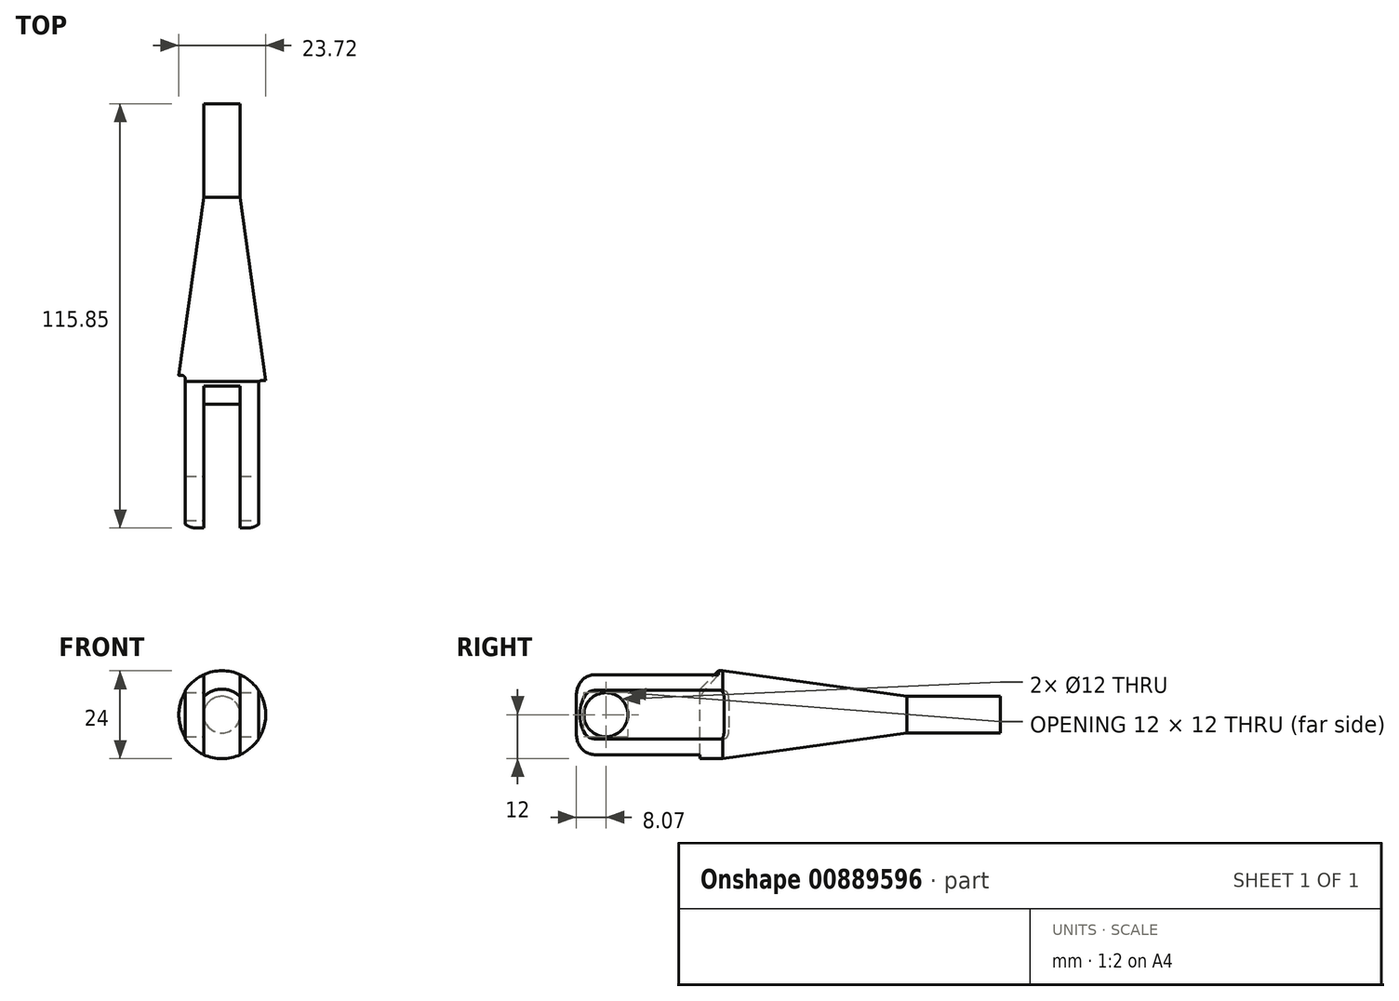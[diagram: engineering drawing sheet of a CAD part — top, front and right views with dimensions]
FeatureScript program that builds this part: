
annotation { "Feature Type Name" : "Feature", "Feature Type Description" : "" }
export const myFeature = defineFeature(function(context is Context, id is Id, definition is map)
    precondition{}
    {
        {
            var Q0;
            Q0=qCreatedBy(makeId("Right.planeOp"),FACE);
            var sketch = newSketch(context, id + "F0", { "sketchPlane" : qUnion([Q0])});
            skLineSegment(sketch, "E0", {"start": v(-22.63, 0) * mm, "end": v(-22.63, 12) * mm});
            skLineSegment(sketch, "E1", {"start": v(-22.63, 12) * mm, "end": v(17.37, 12) * mm});
            skLineSegment(sketch, "E2", {"start": v(93.22, 5) * mm, "end": v(93.22, 0) * mm});
            skLineSegment(sketch, "E3", {"start": v(93.22, 0) * mm, "end": v(-22.63, 0) * mm});
            skLineSegment(sketch, "E4", {"start": v(93.22, 5) * mm, "end": v(67.7, 5) * mm});
            skLineSegment(sketch, "E5", {"start": v(67.7, 5) * mm, "end": v(17.37, 12) * mm});
            skSolve(sketch);
        }
        {
            var Q0;
            Q0=makeQuery(id+"F0.imprint","IMPRINT",FACE,{"disambiguationData":[TD([[makeQuery(id+"F0.imprint","IMPRINT",EDGE,{"derivedFrom":sQuery(id+"F0.wireOp",EDGE,"E0")}),-1.0]])]});
            var Q1;
            Q1=sQuery(id+"F0.wireOp",EDGE,"E3");
            revolve(context, id + "F1", {"surfaceOperationType" : NewSurfaceOperationType.NEW, "entities" : qUnion([Q0]), "axis" : qUnion([Q1]), "revolveType" : RevolveType.FULL});
        }
        {
            var Q0;
            Q0=qCreatedBy(makeId("Top.planeOp"),FACE);
            cPlane(context, id + "F2", {"entities" : qUnion([Q0]), "cplaneType" : CPlaneType.OFFSET, "offset" : 25 * mm, "width" : 150 * mm, "height" : 150 * mm});
        }
        {
            var Q0;
            Q0=qCreatedBy(id+"F2.planeOp",FACE);
            var sketch = newSketch(context, id + "F3", { "sketchPlane" : qUnion([Q0])});
            skLineSegment(sketch, "E6", {"start": v(-10, 19.06) * mm, "end": v(-10, -31.43) * mm});
            skLineSegment(sketch, "E7", {"start": v(10, -31.43) * mm, "end": v(10, 17.7) * mm});
            skLineSegment(sketch, "E8", {"start": v(10, 17.7) * mm, "end": v(28.05, 17.7) * mm});
            skLineSegment(sketch, "E9", {"start": v(28.05, 17.7) * mm, "end": v(28.05, -44.11) * mm});
            skLineSegment(sketch, "E10", {"start": v(28.05, -44.11) * mm, "end": v(-18.09, -44.11) * mm});
            skLineSegment(sketch, "E11", {"start": v(-18.09, -44.11) * mm, "end": v(-18.09, 18.88) * mm});
            skLineSegment(sketch, "E12", {"start": v(-18.09, 18.88) * mm, "end": v(-10, 19.06) * mm});
            skLineSegment(sketch, "E13", {"start": v(-10, -31.43) * mm, "end": v(-5, -31.43) * mm});
            skLineSegment(sketch, "E14", {"start": v(-5, -31.43) * mm, "end": v(-5, 11.16) * mm});
            skLineSegment(sketch, "E15", {"start": v(-5, 11.16) * mm, "end": v(5, 11.16) * mm});
            skLineSegment(sketch, "E16", {"start": v(5, 11.16) * mm, "end": v(5, -31.43) * mm});
            skLineSegment(sketch, "E17", {"start": v(5, -31.43) * mm, "end": v(10, -31.43) * mm});
            skSolve(sketch);
        }
        {
            var Q0;
            Q0=makeQuery(id+"F3.imprint","IMPRINT",FACE,{"disambiguationData":[TD([[makeQuery(id+"F3.imprint","IMPRINT",EDGE,{"derivedFrom":sQuery(id+"F3.wireOp",EDGE,"E6")}),-1.0]])]});
            extrude(context, id + "F4", {"entities" : qUnion([Q0]), "operationType" : NewBodyOperationType.REMOVE, "endBound" : BoundingType.THROUGH_ALL, "oppositeDirection" : true, "depth" : 25 * mm, "offsetDistance" : 25 * mm});
        }
        {
            var Q0;
            Q0=makeQuery(id+"F4.boolean.opBoolean","COPY",FACE,{"derivedFrom":makeQuery(id+"F4.opExtrude","SWEPT_FACE",FACE,{"disambiguationData":[OSD([sQuery(id+"F3.wireOp",EDGE,"E7")])]})});
            var sketch = newSketch(context, id + "F5", { "sketchPlane" : qUnion([Q0])});
            skCircle(sketch, "E18", {"center": v(-14.56, 0) * mm, "radius": 6 * mm});
            skSolve(sketch);
        }
        {
            var Q0;
            Q0=makeQuery(id+"F5.imprint","IMPRINT",FACE,{"disambiguationData":[TD([[makeQuery(id+"F5.imprint","IMPRINT",EDGE,{"derivedFrom":sQuery(id+"F5.wireOp",EDGE,"E18")}),1.0]])]});
            extrude(context, id + "F6", {"entities" : qUnion([Q0]), "operationType" : NewBodyOperationType.REMOVE, "endBound" : BoundingType.THROUGH_ALL, "oppositeDirection" : true, "depth" : 25 * mm, "offsetDistance" : 25 * mm});
        }
        {
            var Q0;
            Q0=makeQuery(id+"F4.boolean.opBoolean","INTERSECT",EDGE,{"disambiguationData":[OD(1.0)],"derivedFrom":[makeQuery(id+"F1.opRevolve","SWEPT_FACE",FACE,{"disambiguationData":[OSD([sQuery(id+"F0.wireOp",EDGE,"E1")])]}),makeQuery(id+"F4.opExtrude","SWEPT_FACE",FACE,{"disambiguationData":[OSD([sQuery(id+"F3.wireOp",EDGE,"E15")])]})]});
            chamfer(context, id + "F7", {"entities" : qUnion([Q0]), "width" : 5 * mm, "tangentPropagation" : true});
        }
        {
            var Q0;
            {var subQ0=sQuery(id+"F0.wireOp",EDGE,"E0");var subQ1=sQuery(id+"F0.wireOp",EDGE,"E1");Q0=makeQuery(id+"F4.boolean.opBoolean","SPLIT",EDGE,{"disambiguationData":[TD([makeQuery(id+"F1.opRevolve","SWEPT_FACE",FACE,{"disambiguationData":[OSD([subQ0])]}),makeQuery(id+"F1.opRevolve","SWEPT_FACE",FACE,{"disambiguationData":[OSD([subQ1])]}),makeQuery(id+"F4.opExtrude","SWEPT_FACE",FACE,{"disambiguationData":[OSD([sQuery(id+"F3.wireOp",EDGE,"E6")])]}),makeQuery(id+"F4.opExtrude","SWEPT_FACE",FACE,{"disambiguationData":[OSD([sQuery(id+"F3.wireOp",EDGE,"E14")])]})]),OD(1.0)],"derivedFrom":makeQuery(id+"F1.opRevolve","SWEPT_EDGE",EDGE,{"disambiguationData":[OSD([subQ0,subQ1])]})});}
            var Q1;
            {var subQ0=sQuery(id+"F0.wireOp",EDGE,"E0");var subQ1=sQuery(id+"F0.wireOp",EDGE,"E1");Q1=makeQuery(id+"F4.boolean.opBoolean","SPLIT",EDGE,{"disambiguationData":[TD([makeQuery(id+"F1.opRevolve","SWEPT_FACE",FACE,{"disambiguationData":[OSD([subQ0])]}),makeQuery(id+"F1.opRevolve","SWEPT_FACE",FACE,{"disambiguationData":[OSD([subQ1])]}),makeQuery(id+"F4.opExtrude","SWEPT_FACE",FACE,{"disambiguationData":[OSD([sQuery(id+"F3.wireOp",EDGE,"E7")])]}),makeQuery(id+"F4.opExtrude","SWEPT_FACE",FACE,{"disambiguationData":[OSD([sQuery(id+"F3.wireOp",EDGE,"E16")])]})]),OD(1.0)],"derivedFrom":makeQuery(id+"F1.opRevolve","SWEPT_EDGE",EDGE,{"disambiguationData":[OSD([subQ0,subQ1])]})});}
            var Q2;
            Q2=makeQuery(id+"F1.opRevolve","SWEPT_EDGE",EDGE,{"disambiguationData":[OSD([sQuery(id+"F0.wireOp",EDGE,"fQOMSYzY-wmGP-pXEB-7GxN-5RBEn2TgBpH8"),sQuery(id+"F0.wireOp",EDGE,"4NhgvXhO-ehyN-Uv1U-nfto-ZAYPEsYbR0pX")])]});
            fillet(context, id + "F8", {"entities" : qUnion([Q0, Q1, Q2]), "radius" : 5 * mm, "tangentPropagation" : true, "allowEdgeOverflow" : false});
        }
        {
            var Q0;
            Q0=makeQuery(id+"F4.boolean.opBoolean","COPY",EDGE,{"derivedFrom":makeQuery(id+"F4.opExtrude","SWEPT_EDGE",EDGE,{"disambiguationData":[OSD([sQuery(id+"F3.wireOp",EDGE,"E7"),sQuery(id+"F3.wireOp",EDGE,"E8")])]})});
            var Q1;
            Q1=makeQuery(id+"F4.boolean.opBoolean","COPY",EDGE,{"derivedFrom":makeQuery(id+"F4.opExtrude","SWEPT_EDGE",EDGE,{"disambiguationData":[OSD([sQuery(id+"F3.wireOp",EDGE,"E6"),sQuery(id+"F3.wireOp",EDGE,"E12")])]})});
            fillet(context, id + "F9", {"entities" : qUnion([Q0, Q1]), "radius" : 1 * mm, "tangentPropagation" : true, "allowEdgeOverflow" : false});
        }
    });
